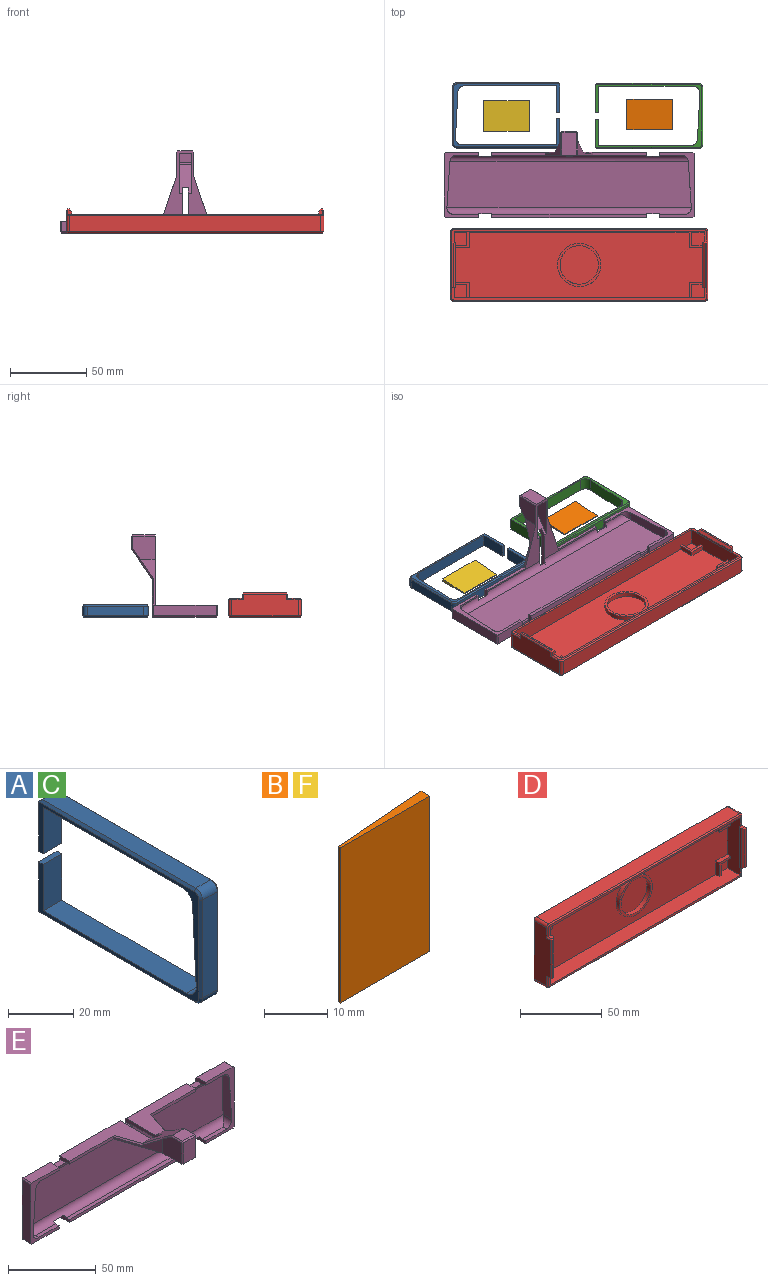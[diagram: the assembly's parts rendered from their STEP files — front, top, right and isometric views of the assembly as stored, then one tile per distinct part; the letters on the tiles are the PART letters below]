
ASSEMBLY  parts=6 mates=5
PART A: 30 faces, bbox 8x70.4x42.8 mm
  f0: plane 60.38x8mm, normal (0,0,-1), area 483.1mm2, adj f1,f13,f14,f15
  f1: plane 17.4x8mm, normal (0,-1,0), area 139.2mm2, adj f0,f2,f14,f15
  f2: plane 8x2mm, normal (0,0,-1), area 16mm2, adj f1,f3,f14,f15
  f3: plane 18.6x8mm, normal (0,1,0), area 148.8mm2, adj f2,f14,f15,f28
  f4: plane 66.56x6.4mm, normal (0,0,1), area 426mm2, adj f16,f26,f28,f29
  f5: plane 36.8x6.4mm, normal (0,-1,0), area 235.5mm2, adj f16,f17,f22,f25
  f6: plane 66.56x6.4mm, normal (0,0,-1), area 426mm2, adj f17,f18,f19,f21
  f7: plane 18.6x8mm, normal (0,1,0), area 148.8mm2, adj f8,f14,f15,f19
  f8: plane 8x2mm, normal (0,0,1), area 16mm2, adj f7,f9,f14,f15
  f9: plane 17.4x8mm, normal (0,-1,0), area 139.2mm2, adj f8,f10,f14,f15
  f10: plane 61.96x8mm, normal (0,0,1), area 495.7mm2, adj f9,f11,f14,f15
  f11: cylinder r=4.4mm len=8mm, axis (-1,0,0), area 57.1mm2, adj f10,f12,f14,f15
  f12: plane 30x8mm, normal (0,1,-0.05), area 240.3mm2, adj f11,f13,f14,f15
  f13: cylinder r=4.4mm len=8mm, axis (-1,0,0), area 53.4mm2, adj f0,f12,f14,f15
  f14: plane 69.56x41.2mm, normal (1,0,0), area 319.6mm2, adj f0,f1,f2,f3,f7,f8,f9,f10
  f15: plane 69.56x41.2mm, normal (-1,0,0), area 319.6mm2, adj f0,f1,f2,f3,f7,f8,f9,f10
  f16: cylinder r=3mm len=6.4mm, axis (1,0,0), area 30.2mm2, adj f4,f5,f24,f27
  f17: cylinder r=3mm len=6.4mm, axis (-1,0,0), area 30.2mm2, adj f5,f6,f20,f23
  f18: plane 67.36x0.8mm, normal (0.71,0,-0.71), area 75.8mm2, adj f6,f14,f19,f20
  f19: plane 8x0.8mm, normal (0,0.71,-0.71), area 8.1mm2, adj f6,f7,f18,f21
  f20: cone r=2.2mm half-angle=45deg, axis (-1,0,0), area 4.6mm2, adj f14,f17,f18,f22
  f21: plane 67.36x0.8mm, normal (-0.71,0,-0.71), area 75.8mm2, adj f6,f15,f19,f23
  f22: plane 36.8x0.8mm, normal (0.71,-0.71,0), area 41.6mm2, adj f5,f14,f20,f24
  f23: cone r=2.2mm half-angle=45deg, axis (1,0,0), area 4.6mm2, adj f15,f17,f21,f25
  f24: cone r=2.2mm half-angle=45deg, axis (-1,0,0), area 4.6mm2, adj f14,f16,f22,f26
  f25: plane 36.8x0.8mm, normal (-0.71,-0.71,0), area 41.6mm2, adj f5,f15,f23,f27
  f26: plane 67.36x0.8mm, normal (0.71,0,0.71), area 75.8mm2, adj f4,f14,f24,f28
  f27: cone r=2.2mm half-angle=45deg, axis (1,0,0), area 4.6mm2, adj f15,f16,f25,f29
  f28: plane 8x0.8mm, normal (0,0.71,0.71), area 8.1mm2, adj f3,f4,f26,f29
  f29: plane 67.36x0.8mm, normal (-0.71,0,0.71), area 75.8mm2, adj f4,f15,f27,f28
PART B: 6 faces, bbox 20x2x30 mm
  f0: plane 30x0.5mm, normal (-1,0,0), area 15mm2, adj f1,f3,f4,f5
  f1: plane 20x2mm, normal (0,0,1), area 25mm2, adj f0,f2,f4,f5
  f2: plane 30x2mm, normal (1,0,0), area 60mm2, adj f1,f3,f4,f5
  f3: plane 20x2mm, normal (0,0,-1), area 25mm2, adj f0,f2,f4,f5
  f4: plane 30x20mm, normal (0,-1,0), area 600mm2, adj f0,f1,f2,f3
  f5: plane 30x20mm, normal (-0.07,1,0), area 601.7mm2, adj f0,f1,f2,f3
PART C: same geometry as A
PART D: 88 faces, bbox 168.8x15.9x47.6 mm
  f0: plane 43.2x11mm, normal (-1,0,0), area 457.1mm2, adj f1,f2,f3,f4,f5,f17,f18,f20
  f1: plane 8.6x8.4mm, normal (0,-1,0), area 72.2mm2, adj f0,f3,f41,f44
  f2: plane 164x43.2mm, normal (0,-1,0), area 6043.3mm2, adj f0,f3,f5,f7,f23,f28,f29,f33
  f3: plane 164x11.2mm, normal (0,0,1), area 1796.1mm2, adj f0,f1,f2,f6,f7,f21,f32,f33
  f4: plane 8.6x8.4mm, normal (0,-1,0), area 72.2mm2, adj f0,f5,f36,f37
  f5: plane 164x11.2mm, normal (0,0,-1), area 1796.1mm2, adj f0,f2,f4,f7,f8,f20,f26,f29
  f6: plane 8.6x8.4mm, normal (0,-1,0), area 72.2mm2, adj f3,f7,f31,f32
  f7: plane 43.2x11.2mm, normal (1,0,0), area 460.6mm2, adj f2,f3,f5,f6,f8,f14,f15,f20
  f8: plane 8.6x8.4mm, normal (0,-1,0), area 72.2mm2, adj f5,f7,f26,f27
  f9: plane 43.6x14.3mm, normal (-1,0,0), area 570.3mm2, adj f46,f48,f56,f58,f63,f69,f71,f86
  f10: plane 164.8x10.8mm, normal (0,0,-1), area 1779.8mm2, adj f48,f49,f76,f85
  f11: plane 43.6x14.3mm, normal (1,0,0), area 570.3mm2, adj f47,f49,f65,f68,f73,f77,f79,f81
  f12: plane 164.8x10.8mm, normal (0,0,1), area 1779.8mm2, adj f46,f47,f60,f82
  f13: plane 167.2x46mm, normal (0,1,0), area 7690mm2, adj f80,f81,f82,f83,f84,f85,f86,f87
  f14: plane 2.98x2.6mm, normal (0,0,-1), area 6.6mm2, adj f7,f21,f50,f54,f55,f64,f69
  f15: plane 2.98x2.6mm, normal (0,0,1), area 6.6mm2, adj f7,f20,f50,f54,f55,f58,f59
  f16: plane 28.4x1.1mm, normal (0,-1,0), area 31.2mm2, adj f54,f59,f63,f64
  f17: plane 2.98x2.6mm, normal (0,0,-1), area 6.6mm2, adj f0,f21,f51,f52,f53,f72,f77
  f18: plane 2.98x2.6mm, normal (0,0,1), area 6.6mm2, adj f0,f20,f51,f52,f53,f67,f68
  f19: plane 28.4x1.1mm, normal (0,-1,0), area 31.2mm2, adj f53,f67,f72,f73
  f20: plane 167.2x8mm, normal (0,-1,0), area 254.6mm2, adj f0,f5,f7,f15,f18,f56,f57,f60
  f21: plane 167.2x8mm, normal (0,-1,0), area 254.6mm2, adj f0,f3,f7,f14,f17,f71,f74,f76
  f22: cylinder r=12.6mm len=25.2mm, axis (0,1,0), area 237.5mm2, adj f24,f25
  f23: cylinder r=14.2mm len=28.4mm, axis (0,1,0), area 267.7mm2, adj f2,f24
  f24: plane 28.4x28.4mm, normal (0,-1,0), area 134.7mm2, adj f22,f23
  f25: plane 25.2x25.2mm, normal (0,-1,0), area 498.8mm2, adj f22
  f26: plane 8.6x3.2mm, normal (-1,0,0), area 27.5mm2, adj f5,f8,f27,f30
  f27: plane 8.4x3.2mm, normal (0,0,1), area 26.9mm2, adj f7,f8,f26,f30
  f28: plane 10x3mm, normal (0,0,-1), area 30mm2, adj f2,f7,f29,f30
  f29: plane 10.2x3mm, normal (1,0,0), area 30.6mm2, adj f2,f5,f28,f30
  f30: plane 10.2x10mm, normal (0,-1,0), area 29.8mm2, adj f5,f7,f26,f27,f28,f29
  f31: plane 8.4x3.2mm, normal (0,0,-1), area 26.9mm2, adj f6,f7,f32,f35
  f32: plane 8.6x3.2mm, normal (-1,0,0), area 27.5mm2, adj f3,f6,f31,f35
  f33: plane 10.2x3mm, normal (1,0,0), area 30.6mm2, adj f2,f3,f34,f35
  f34: plane 10x3mm, normal (0,0,1), area 30mm2, adj f2,f7,f33,f35
  f35: plane 10.2x10mm, normal (0,-1,0), area 29.8mm2, adj f3,f7,f31,f32,f33,f34
  f36: plane 8.4x3mm, normal (0,0,1), area 25.2mm2, adj f0,f4,f37,f40
  f37: plane 8.6x3mm, normal (1,0,0), area 25.8mm2, adj f4,f5,f36,f40
  f38: plane 10.2x3mm, normal (-1,0,0), area 30.6mm2, adj f2,f5,f39,f40
  f39: plane 10x3mm, normal (0,0,-1), area 30mm2, adj f0,f2,f38,f40
  f40: plane 10.2x10mm, normal (0,-1,0), area 29.8mm2, adj f0,f5,f36,f37,f38,f39
  f41: plane 8.4x3mm, normal (0,0,-1), area 25.2mm2, adj f0,f1,f44,f45
  f42: plane 10x3mm, normal (0,0,1), area 30mm2, adj f0,f2,f43,f45
  f43: plane 10.2x3mm, normal (-1,0,0), area 30.6mm2, adj f2,f3,f42,f45
  f44: plane 8.6x3mm, normal (1,0,0), area 25.8mm2, adj f1,f3,f41,f45
  f45: plane 10.2x10mm, normal (0,-1,0), area 29.8mm2, adj f0,f3,f41,f42,f43,f44
  f46: cylinder r=2mm len=10.8mm, axis (0,-1,0), area 33.9mm2, adj f9,f12,f57,f84
  f47: cylinder r=2mm len=10.8mm, axis (0,1,0), area 33.9mm2, adj f11,f12,f62,f80
  f48: cylinder r=2mm len=10.8mm, axis (0,1,0), area 33.9mm2, adj f9,f10,f74,f87
  f49: cylinder r=2mm len=10.8mm, axis (0,-1,0), area 33.9mm2, adj f10,f11,f78,f83
  f50: plane 30x1.28mm, normal (1,0,0), area 38.5mm2, adj f14,f15,f54,f55
  f51: plane 30x1.28mm, normal (-1,0,0), area 38.5mm2, adj f17,f18,f52,f53
  f52: plane 30x1mm, normal (-0.71,0.71,0), area 42.4mm2, adj f0,f17,f18,f51
  f53: plane 30x1.5mm, normal (-0.71,-0.71,0), area 62.7mm2, adj f17,f18,f19,f51,f67,f72
  f54: plane 30x1.5mm, normal (0.71,-0.71,0), area 62.7mm2, adj f14,f15,f16,f50,f59,f64
  f55: plane 30x1mm, normal (0.71,0.71,0), area 42.4mm2, adj f7,f14,f15,f50
  f56: plane 7.6x0.8mm, normal (-0.71,-0.71,0), area 8.1mm2, adj f9,f20,f57,f58
  f57: cone r=1.2mm half-angle=45deg, axis (0,1,0), area 2.8mm2, adj f20,f46,f56,f60
  f58: plane 3.5x0.8mm, normal (-0.71,0,0.71), area 3.5mm2, adj f9,f15,f56,f61
  f59: plane 1.9x0.8mm, normal (0,-0.71,0.71), area 1.7mm2, adj f15,f16,f54,f61
  f60: plane 164.8x0.8mm, normal (0,-0.71,0.71), area 186.4mm2, adj f12,f20,f57,f62
  f61: plane 0.8x0.8mm, normal (-0.58,-0.58,0.58), area 0.6mm2, adj f58,f59,f63
  f62: cone r=1.2mm half-angle=45deg, axis (0,1,0), area 2.8mm2, adj f20,f47,f60,f65
  f63: plane 28.4x0.8mm, normal (-0.71,-0.71,0), area 32.1mm2, adj f9,f16,f61,f66
  f64: plane 1.9x0.8mm, normal (0,-0.71,-0.71), area 1.7mm2, adj f14,f16,f54,f66
  f65: plane 7.6x0.8mm, normal (0.71,-0.71,0), area 8.1mm2, adj f11,f20,f62,f68
  f66: plane 0.8x0.8mm, normal (-0.58,-0.58,-0.58), area 0.6mm2, adj f63,f64,f69
  f67: plane 1.9x0.8mm, normal (0,-0.71,0.71), area 1.7mm2, adj f18,f19,f53,f70
  f68: plane 3.5x0.8mm, normal (0.71,0,0.71), area 3.5mm2, adj f11,f18,f65,f70
  f69: plane 3.5x0.8mm, normal (-0.71,0,-0.71), area 3.5mm2, adj f9,f14,f66,f71
  f70: plane 0.8x0.8mm, normal (0.58,-0.58,0.58), area 0.6mm2, adj f67,f68,f73
  f71: plane 7.6x0.8mm, normal (-0.71,-0.71,0), area 8.1mm2, adj f9,f21,f69,f74
  f72: plane 1.9x0.8mm, normal (0,-0.71,-0.71), area 1.7mm2, adj f17,f19,f53,f75
  f73: plane 28.4x0.8mm, normal (0.71,-0.71,0), area 32.1mm2, adj f11,f19,f70,f75
  f74: cone r=1.2mm half-angle=45deg, axis (0,1,0), area 2.8mm2, adj f21,f48,f71,f76
  f75: plane 0.8x0.8mm, normal (0.58,-0.58,-0.58), area 0.6mm2, adj f72,f73,f77
  f76: plane 164.8x0.8mm, normal (0,-0.71,-0.71), area 186.4mm2, adj f10,f21,f74,f78
  f77: plane 3.5x0.8mm, normal (0.71,0,-0.71), area 3.5mm2, adj f11,f17,f75,f79
  f78: cone r=1.2mm half-angle=45deg, axis (0,1,0), area 2.8mm2, adj f21,f49,f76,f79
  f79: plane 7.6x0.8mm, normal (0.71,-0.71,0), area 8.1mm2, adj f11,f21,f77,f78
  f80: cone r=1.2mm half-angle=45deg, axis (0,-1,0), area 2.8mm2, adj f13,f47,f81,f82
  f81: plane 43.6x0.8mm, normal (0.71,0.71,0), area 49.3mm2, adj f11,f13,f80,f83
  f82: plane 164.8x0.8mm, normal (0,0.71,0.71), area 186.4mm2, adj f12,f13,f80,f84
  f83: cone r=1.2mm half-angle=45deg, axis (0,-1,0), area 2.8mm2, adj f13,f49,f81,f85
  f84: cone r=1.2mm half-angle=45deg, axis (0,-1,0), area 2.8mm2, adj f13,f46,f82,f86
  f85: plane 164.8x0.8mm, normal (0,0.71,-0.71), area 186.4mm2, adj f10,f13,f83,f87
  f86: plane 43.6x0.8mm, normal (-0.71,0.71,0), area 49.3mm2, adj f9,f13,f84,f87
  f87: cone r=1.2mm half-angle=45deg, axis (0,-1,0), area 2.8mm2, adj f13,f48,f85,f86
PART E: 96 faces, bbox 164x54x56.4 mm
  f0: plane 18.64x12.68mm, normal (0,-0.56,-0.83), area 161.8mm2, adj f3,f38,f39,f68,f73,f76,f77
  f1: plane 19.8x17.81mm, normal (0,0.56,0.83), area 264mm2, adj f2,f12,f38,f39,f68,f81,f82,f85
  f2: plane 48.8x24.24mm, normal (0,0,1), area 515.7mm2, adj f1,f4,f27,f38,f56,f83,f85
  f3: plane 101.6x47.01mm, normal (0,0,-1), area 620.5mm2, adj f0,f4,f5,f9,f27,f29,f38,f39
  f4: plane 36.14x2mm, normal (0,-1,0), area 70.9mm2, adj f2,f3,f27,f78,f83
  f5: cylinder r=4.4mm len=156.3mm, axis (-1,0,0), area 970.9mm2, adj f3,f6,f14,f15,f26,f27,f28,f29
  f6: plane 160.24x30mm, normal (0,-1,-0.05), area 4754.7mm2, adj f5,f7,f42,f43,f44,f45
  f7: cylinder r=4.4mm len=160.26mm, axis (-1,0,0), area 1083.5mm2, adj f6,f8,f10,f20,f32,f33,f34,f35
  f8: plane 16.53x2.58mm, normal (0,0,1), area 42.6mm2, adj f7,f19,f36,f44
  f9: plane 36.14x2mm, normal (0,-1,0), area 70.9mm2, adj f3,f12,f29,f79,f80
  f10: plane 101.6x2.58mm, normal (0,0,1), area 262mm2, adj f7,f11,f33,f37
  f11: plane 101.6x2mm, normal (0,-1,0), area 203.2mm2, adj f10,f17,f33,f37
  f12: plane 48.8x25.04mm, normal (0,0,1), area 554.8mm2, adj f1,f9,f23,f29,f39,f80,f81
  f13: plane 22x7.17mm, normal (0,0,1), area 157.8mm2, adj f19,f26,f62,f64
  f14: plane 14.55x1mm, normal (0,0,-1), area 14.6mm2, adj f5,f21,f30,f41
  f15: plane 14.55x1mm, normal (0,0,-1), area 14.6mm2, adj f5,f19,f26,f46
  f16: plane 22x7.17mm, normal (0,0,-1), area 157.8mm2, adj f19,f36,f58,f59
  f17: plane 101.6x7.17mm, normal (0,0,-1), area 728.8mm2, adj f11,f33,f37,f66
  f18: plane 22x7.17mm, normal (0,0,1), area 157.8mm2, adj f21,f30,f51,f54
  f19: plane 42.8x22.8mm, normal (0,-1,0), area 209.5mm2, adj f8,f13,f15,f16,f24,f26,f36,f44
  f20: plane 16.53x2.58mm, normal (0,0,1), area 42.6mm2, adj f7,f21,f34,f43
  f21: plane 42.8x22.8mm, normal (0,-1,0), area 209.5mm2, adj f14,f18,f20,f22,f25,f30,f34,f41
  f22: plane 22x7.17mm, normal (0,0,-1), area 157.8mm2, adj f21,f34,f48,f49
  f23: plane 162.4x42mm, normal (0,1,0), area 6630.6mm2, adj f12,f26,f27,f29,f30,f33,f34,f36
  f24: plane 41.2x7.17mm, normal (1,0,0), area 295.5mm2, adj f19,f59,f61,f62
  f25: plane 41.2x7.17mm, normal (-1,0,0), area 295.5mm2, adj f21,f48,f51,f52
  f26: plane 7.97x3.4mm, normal (-1,0,0), area 19.2mm2, adj f5,f13,f15,f19,f23,f28,f57,f64
  f27: plane 7.97x3.4mm, normal (1,0,0), area 19.2mm2, adj f2,f3,f4,f5,f23,f28,f56,f57
  f28: plane 8.4x3.96mm, normal (0,0,1), area 33.2mm2, adj f5,f26,f27,f57
  f29: plane 7.97x3.4mm, normal (-1,0,0), area 19.6mm2, adj f3,f5,f9,f12,f23,f31,f55
  f30: plane 7.97x3.4mm, normal (1,0,0), area 19.2mm2, adj f5,f14,f18,f21,f23,f31,f54,f55
  f31: plane 8.4x3.96mm, normal (0,0,1), area 33.2mm2, adj f5,f29,f30,f55
  f32: plane 8.4x2.38mm, normal (0,0,-1), area 20mm2, adj f7,f33,f34,f67
  f33: plane 7.97x3.4mm, normal (-1,0,0), area 18.3mm2, adj f7,f10,f11,f17,f23,f32,f66,f67
  f34: plane 7.97x3.4mm, normal (1,0,0), area 18.3mm2, adj f7,f20,f21,f22,f23,f32,f49,f67
  f35: plane 8.4x2.38mm, normal (0,0,-1), area 20mm2, adj f7,f36,f37,f65
  f36: plane 7.97x3.4mm, normal (-1,0,0), area 18.3mm2, adj f7,f8,f16,f19,f23,f35,f58,f65
  f37: plane 7.97x3.4mm, normal (1,0,0), area 18.3mm2, adj f7,f10,f11,f17,f23,f35,f65,f66
  f38: plane 29.97x7.33mm, normal (-1,0,0), area 69.2mm2, adj f0,f1,f2,f3,f5,f23,f40,f47
  f39: plane 29.97x7.33mm, normal (1,0,0), area 69.5mm2, adj f0,f1,f3,f5,f12,f23,f40,f47
  f40: plane 4x3.38mm, normal (0,0,1), area 13.5mm2, adj f5,f38,f39,f47
  f41: cylinder r=4.4mm len=5.39mm, axis (0,1,0), area 24.7mm2, adj f5,f14,f21,f42
  f42: plane 30x6.97mm, normal (1,0,-0.07), area 185.8mm2, adj f5,f6,f21,f41,f43
  f43: cylinder r=4.4mm len=6.98mm, axis (0,1,0), area 39.2mm2, adj f6,f7,f20,f21,f42
  f44: cylinder r=4.4mm len=6.98mm, axis (0,1,0), area 39.2mm2, adj f6,f7,f8,f19,f45
  f45: plane 30x6.97mm, normal (-1,0,-0.07), area 185.8mm2, adj f5,f6,f19,f44,f46
  f46: cylinder r=4.4mm len=5.39mm, axis (0,1,0), area 24.7mm2, adj f5,f15,f19,f45
  f47: plane 4x0.8mm, normal (0,0.71,0.71), area 4.5mm2, adj f23,f38,f39,f40
  f48: plane 7.17x0.8mm, normal (-0.71,0,-0.71), area 8.1mm2, adj f21,f22,f25,f50
  f49: plane 22x0.8mm, normal (0,0.71,-0.71), area 24.9mm2, adj f22,f23,f34,f50
  f50: plane 0.8x0.8mm, normal (-0.58,0.58,-0.58), area 0.6mm2, adj f48,f49,f52
  f51: plane 7.17x0.8mm, normal (-0.71,0,0.71), area 8.1mm2, adj f18,f21,f25,f53
  f52: plane 41.2x0.8mm, normal (-0.71,0.71,0), area 46.6mm2, adj f23,f25,f50,f53
  f53: plane 0.8x0.8mm, normal (-0.58,0.58,0.58), area 0.6mm2, adj f51,f52,f54
  f54: plane 22x0.8mm, normal (0,0.71,0.71), area 24.9mm2, adj f18,f23,f30,f53
  f55: plane 8.4x0.8mm, normal (0,0.71,0.71), area 9.5mm2, adj f23,f29,f30,f31
  f56: plane 48.8x0.8mm, normal (0,0.71,0.71), area 55.2mm2, adj f2,f23,f27,f38
  f57: plane 8.4x0.8mm, normal (0,0.71,0.71), area 9.5mm2, adj f23,f26,f27,f28
  f58: plane 22x0.8mm, normal (0,0.71,-0.71), area 24.9mm2, adj f16,f23,f36,f60
  f59: plane 7.17x0.8mm, normal (0.71,0,-0.71), area 8.1mm2, adj f16,f19,f24,f60
  f60: plane 0.8x0.8mm, normal (0.58,0.58,-0.58), area 0.6mm2, adj f58,f59,f61
  f61: plane 41.2x0.8mm, normal (0.71,0.71,0), area 46.6mm2, adj f23,f24,f60,f63
  f62: plane 7.17x0.8mm, normal (0.71,0,0.71), area 8.1mm2, adj f13,f19,f24,f63
  f63: plane 0.8x0.8mm, normal (0.58,0.58,0.58), area 0.6mm2, adj f61,f62,f64
  f64: plane 22x0.8mm, normal (0,0.71,0.71), area 24.9mm2, adj f13,f23,f26,f63
  f65: plane 8.4x0.8mm, normal (0,0.71,-0.71), area 9.5mm2, adj f23,f35,f36,f37
  f66: plane 101.6x0.8mm, normal (0,0.71,-0.71), area 114.9mm2, adj f17,f23,f33,f37
  f67: plane 8.4x0.8mm, normal (0,0.71,-0.71), area 9.5mm2, adj f23,f32,f33,f34
  f68: plane 4x2.93mm, normal (0,1,0), area 11.7mm2, adj f0,f1,f38,f39
  f69: plane 9.4x8.15mm, normal (0,0,1), area 76.6mm2, adj f87,f88,f92,f93
  f70: plane 14.8x9.4mm, normal (0,-1,0), area 139.1mm2, adj f3,f86,f92,f95
  f71: plane 15.66x14.8mm, normal (1,0,0), area 208.2mm2, adj f3,f78,f85,f89,f93,f95
  f72: plane 15.66x14.8mm, normal (-1,0,0), area 208.2mm2, adj f3,f79,f81,f82,f86,f87
  f73: plane 8x1.6mm, normal (0,-0.64,-0.77), area 16.6mm2, adj f0,f74,f76,f77
  f74: plane 8x6mm, normal (0,0,-1), area 48mm2, adj f73,f75,f76,f77
  f75: plane 14x8mm, normal (0,1,0), area 112mm2, adj f3,f74,f76,f77
  f76: plane 26.24x14mm, normal (1,0,0), area 223.5mm2, adj f0,f3,f73,f74,f75
  f77: plane 26.24x14mm, normal (-1,0,0), area 223.5mm2, adj f0,f3,f73,f74,f75
  f78: plane 30x10mm, normal (0.95,-0.32,0), area 95.7mm2, adj f3,f4,f71,f83,f85
  f79: plane 30x10mm, normal (-0.95,-0.32,0), area 95.7mm2, adj f3,f9,f72,f80,f81
  f80: plane 17.31x6.53mm, normal (-0.67,-0.22,0.71), area 20.5mm2, adj f9,f12,f79,f81
  f81: plane 13.19x9.38mm, normal (-0.74,0.19,0.64), area 19.1mm2, adj f1,f12,f72,f79,f80,f82
  f82: plane 7.64x5.77mm, normal (-0.71,0.4,0.58), area 10.1mm2, adj f1,f72,f81,f84
  f83: plane 17.31x6.53mm, normal (0.67,-0.22,0.71), area 20.5mm2, adj f2,f4,f78,f85
  f84: plane 0.8x0.8mm, normal (-0.69,0.21,0.69), area 0.3mm2, adj f82,f87,f88
  f85: plane 13.19x9.38mm, normal (0.74,0.19,0.64), area 19.1mm2, adj f1,f2,f71,f78,f83,f89
  f86: plane 14.8x0.8mm, normal (-0.71,-0.71,0), area 16.7mm2, adj f3,f70,f72,f90
  f87: plane 8.15x0.8mm, normal (-0.71,0,0.71), area 9.2mm2, adj f69,f72,f84,f90
  f88: plane 9.4x0.45mm, normal (0,0.29,0.96), area 4.4mm2, adj f1,f69,f84,f91
  f89: plane 7.64x5.77mm, normal (0.71,0.4,0.58), area 10.1mm2, adj f1,f71,f85,f91
  f90: plane 0.8x0.8mm, normal (-0.58,-0.58,0.58), area 0.6mm2, adj f86,f87,f92
  f91: plane 0.8x0.8mm, normal (0.69,0.21,0.69), area 0.3mm2, adj f88,f89,f93
  f92: plane 9.4x0.8mm, normal (0,-0.71,0.71), area 10.6mm2, adj f69,f70,f90,f94
  f93: plane 8.15x0.8mm, normal (0.71,0,0.71), area 9.2mm2, adj f69,f71,f91,f94
  f94: plane 0.8x0.8mm, normal (0.58,-0.58,0.58), area 0.6mm2, adj f92,f93,f95
  f95: plane 14.8x0.8mm, normal (0.71,-0.71,0), area 16.7mm2, adj f3,f70,f71,f94
PART F: same geometry as B
PLACE A rot(axis=(-0.58,-0.58,-0.58),120deg) t=(-48.82,52.79,-38.4)mm
PLACE B rot(axis=(0.58,0.58,0.58),120deg) t=(25.57,-93.2,-20.58)mm
PLACE C rot(axis=(0.58,-0.58,0.58),120deg) t=(47.04,90.41,-38.4)mm
PLACE D rot(axis=(-1,0,0),90deg) t=(0.13,-45.26,74)mm
PLACE E rot(axis=(-1,0,0),90deg) t=(-6.5,7.25,45.78)mm
PLACE F rot(axis=(0.58,0.58,0.58),120deg) t=(-68.36,-93.91,-20.58)mm
MATE planar D.f22 <-> E.f23  axis (0,0,-1) through (0.13,-26.26,12.6)mm
MATE planar B.f4 <-> E.f23  axis (0,0,-1) through (46.37,72.26,12.6)mm
MATE planar A.f15 <-> E.f23  axis (0,0,-1) through (-48.77,72.53,12.6)mm
MATE planar F.f4 <-> E.f23  axis (0,0,-1) through (-47.56,71.55,12.6)mm
MATE planar C.f15 <-> E.f23  axis (0,0,-1) through (77.64,56.17,12.6)mm
